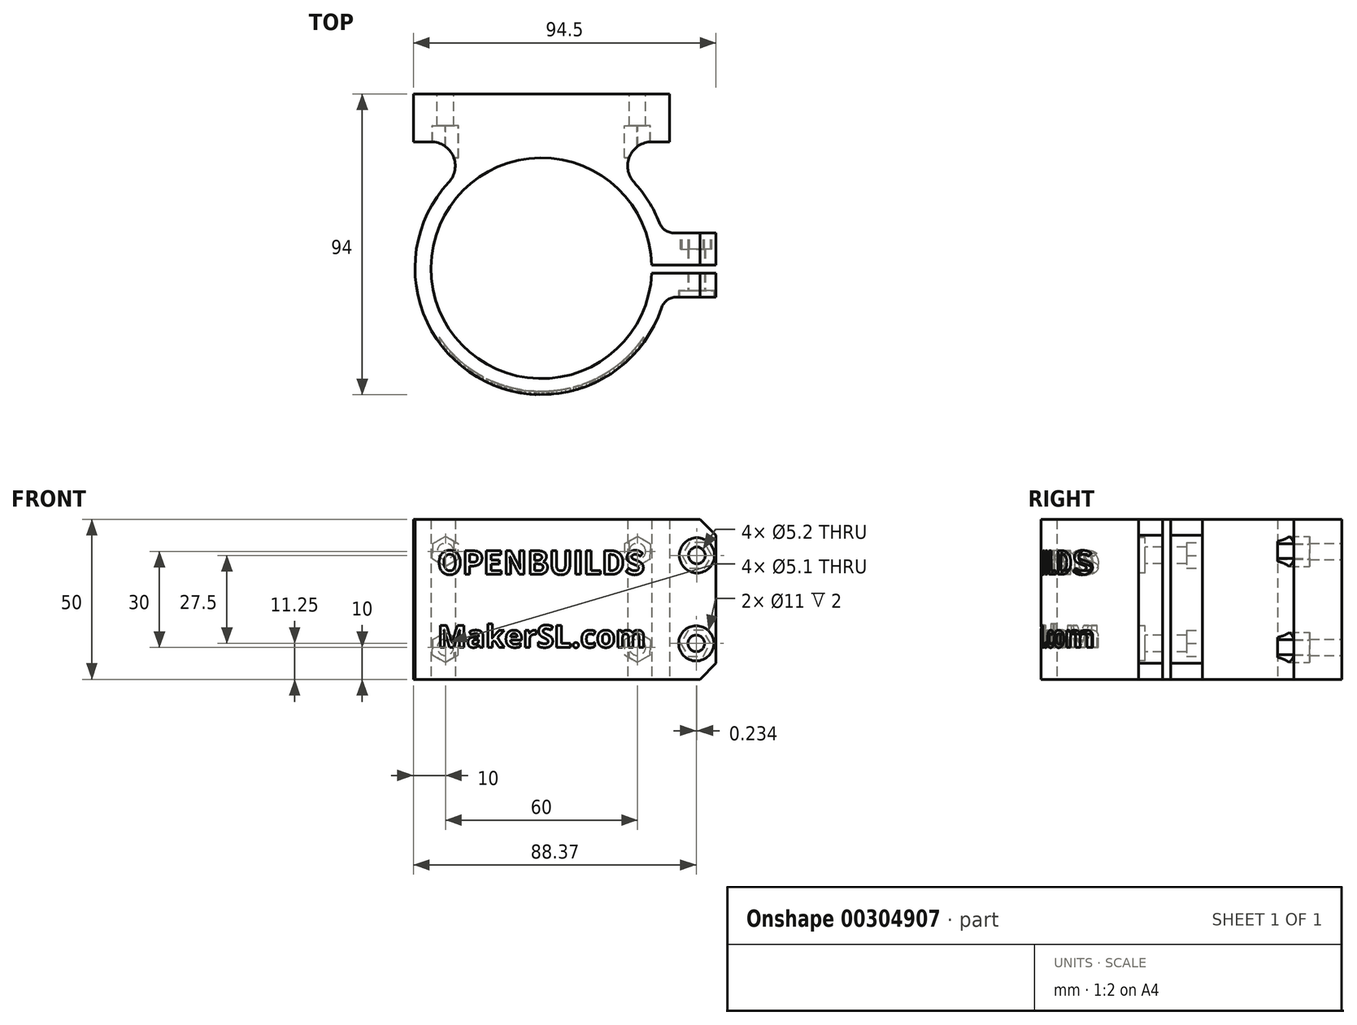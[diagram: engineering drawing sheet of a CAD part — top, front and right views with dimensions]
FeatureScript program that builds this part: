
annotation { "Feature Type Name" : "Feature", "Feature Type Description" : "" }
export const myFeature = defineFeature(function(context is Context, id is Id, definition is map)
    precondition{}
    {
        {
            var Q0;
            Q0=qCreatedBy(makeId("Top.planeOp"),FACE);
            var sketch = newSketch(context, id + "F0", { "sketchPlane" : qUnion([Q0])});
            skArc(sketch, "E0", {"start": v(34.49, 1) * mm, "mid": v(-34.5, 0.25) * mm, "end": v(34.47, -1.5) * mm});
            skArc(sketch, "E1", {"start": v(36.86, 14.2) * mm, "mid": v(33.5, 20.93) * mm, "end": v(28.93, 26.9) * mm});
            skLineSegment(sketch, "E2.bottom", {"start": v(40, 39.5) * mm, "end": v(34.42, 39.5) * mm});
            skLineSegment(sketch, "E2.top", {"start": v(40, 54.5) * mm, "end": v(-40, 54.5) * mm});
            skLineSegment(sketch, "E2.left", {"start": v(40, 39.5) * mm, "end": v(40, 54.5) * mm});
            skLineSegment(sketch, "E2.right", {"start": v(-40, 39.5) * mm, "end": v(-40, 54.5) * mm});
            skPoint(sketch, "E2.middle", {"position": v(0, 47) * mm});
            skLineSegment(sketch, "E3", {"start": v(0, 54.5) * mm, "end": v(0, 34.5) * mm});
            skLineSegment(sketch, "E4.bottom", {"start": v(54.5, -1.5) * mm, "end": v(34.47, -1.5) * mm});
            skLineSegment(sketch, "E4.top", {"start": v(54.5, 1) * mm, "end": v(34.49, 1) * mm});
            skPoint(sketch, "E4.middle", {"position": v(34.5, 0) * mm});
            skLineSegment(sketch, "E5.bottom", {"start": v(54.5, -9) * mm, "end": v(42.24, -9) * mm});
            skLineSegment(sketch, "E5.left", {"start": v(54.5, -9) * mm, "end": v(54.5, -1.5) * mm});
            skLineSegment(sketch, "E6.trimOffspring", {"start": v(54.5, 1) * mm, "end": v(54.5, 8.5) * mm});
            skPoint(sketch, "E7.visualSharp", {"position": v(38.78, 7.5) * mm});
            skPoint(sketch, "E8.visualSharp", {"position": v(38.46, -9) * mm});
            skArc(sketch, "E8.filletArc", {"start": v(42.24, -9) * mm, "mid": v(39.31, -9.95) * mm, "end": v(37.5, -12.43) * mm});
            skArc(sketch, "E9.trimOffspring", {"start": v(-28.93, 26.9) * mm, "mid": v(-20.12, -34) * mm, "end": v(37.5, -12.43) * mm});
            skLineSegment(sketch, "E10.trimOffspring", {"start": v(-34.42, 39.5) * mm, "end": v(-40, 39.5) * mm});
            skArc(sketch, "E11.filletArc", {"start": v(-28.93, 26.9) * mm, "mid": v(-27.55, 35) * mm, "end": v(-34.42, 39.5) * mm});
            skArc(sketch, "E12.filletArc", {"start": v(34.42, 39.5) * mm, "mid": v(27.55, 35) * mm, "end": v(28.93, 26.9) * mm});
            skLineSegment(sketch, "E13.top", {"start": v(54.5, 11) * mm, "end": v(41.52, 11) * mm});
            skLineSegment(sketch, "E13.left", {"start": v(54.5, 8.5) * mm, "end": v(54.5, 11) * mm});
            skPoint(sketch, "E14.visualSharp", {"position": v(37.94, 11) * mm});
            skArc(sketch, "E14.filletArc", {"start": v(36.86, 14.2) * mm, "mid": v(38.7, 11.88) * mm, "end": v(41.52, 11) * mm});
            skSolve(sketch);
        }
        {
            var Q0;
            {var subQ3=sQuery(id+"F0.wireOp",EDGE,"E2.right");Q0=makeQuery(id+"F0.imprint","IMPRINT",FACE,{"disambiguationData":[TD([[makeQuery(id+"F0.imprint","IMPRINT",EDGE,{"derivedFrom":subQ3}),-1.0]])]});}
            var Q1;
            Q1=makeQuery(id+"F0.imprint","IMPRINT",FACE,{"disambiguationData":[TD([[makeQuery(id+"F0.imprint","IMPRINT",EDGE,{"derivedFrom":sQuery(id+"F0.wireOp",EDGE,"E1")}),1.0]])]});
            extrude(context, id + "F1", {"entities" : qUnion([Q0, Q1]), "depth" : 50 * mm});
        }
        {
            var Q0;
            Q0=makeQuery(id+"F1.opExtrude","SWEPT_FACE",FACE,{"disambiguationData":[OSD([sQuery(id+"F0.wireOp",EDGE,"E2.top")])]});
            var sketch = newSketch(context, id + "F2", { "sketchPlane" : qUnion([Q0])});
            skLineSegment(sketch, "E15", {"start": v(-40, 10) * mm, "end": v(40, 10) * mm, "construction": true});
            skLineSegment(sketch, "E16", {"start": v(-40, 40) * mm, "end": v(40, 40) * mm, "construction": true});
            skCircle(sketch, "E17", {"center": v(-30, 10) * mm, "radius": 2.55 * mm});
            skCircle(sketch, "E18", {"center": v(-30, 40) * mm, "radius": 2.55 * mm});
            skCircle(sketch, "E19", {"center": v(30, 40) * mm, "radius": 2.55 * mm});
            skCircle(sketch, "E20", {"center": v(30, 10) * mm, "radius": 2.55 * mm});
            skSolve(sketch);
        }
        {
            var Q0;
            Q0=qSketchRegion(id+"F2",true);
            extrude(context, id + "F3", {"entities" : qUnion([Q0]), "operationType" : NewBodyOperationType.REMOVE, "oppositeDirection" : true, "depth" : 15 * mm});
        }
        {
            var Q0;
            Q0=qCreatedBy(makeId("Front.planeOp"),FACE);
            var sketch = newSketch(context, id + "F4", { "sketchPlane" : qUnion([Q0])});
            skLineSegment(sketch, "E21", {"start": v(0, 25) * mm, "end": v(57.85, 25) * mm});
            skArc(sketch, "E22.0.startCap", {"start": v(0, 22.5) * mm, "mid": v(-2.5, 25) * mm, "end": v(0, 27.5) * mm});
            skArc(sketch, "E22.0.endCap", {"start": v(57.85, 27.5) * mm, "mid": v(60.35, 25) * mm, "end": v(57.85, 22.5) * mm});
            skLineSegment(sketch, "E22.0.left", {"start": v(0, 27.5) * mm, "end": v(57.85, 27.5) * mm});
            skLineSegment(sketch, "E22.0.right", {"start": v(0, 22.5) * mm, "end": v(57.85, 22.5) * mm});
            skSolve(sketch);
        }
        {
            var Q0;
            {var subQ2=sQuery(id+"F0.wireOp",EDGE,"E5.bottom");Q0=makeQuery(id+"FSlxkKbNy0vXjha_1.boolean.opBoolean","SPLIT",FACE,{"disambiguationData":[TD([makeQuery(id+"FSlxkKbNy0vXjha_1.opExtrude","SWEPT_FACE",FACE,{"disambiguationData":[OSD([sQuery(id+"F4.wireOp",EDGE,"E22.0.left")])]})])],"derivedFrom":makeQuery(id+"F1.opExtrude","SWEPT_FACE",FACE,{"disambiguationData":[OSD([subQ2])]})});}
            var sketch = newSketch(context, id + "F5", { "sketchPlane" : qUnion([Q0])});
            skLineSegment(sketch, "E23", {"start": v(48.37, 50) * mm, "end": v(48.37, 0) * mm, "construction": true});
            skLineSegment(sketch, "E24", {"start": v(54.5, 11.25) * mm, "end": v(42.24, 11.25) * mm, "construction": true});
            skCircle(sketch, "E25", {"center": v(48.6, 38.75) * mm, "radius": 2.6 * mm});
            skCircle(sketch, "E26", {"center": v(48.37, 11.25) * mm, "radius": 2.6 * mm});
            skCircle(sketch, "E27", {"center": v(48.6, 38.75) * mm, "radius": 2 * mm});
            skCircle(sketch, "E28", {"center": v(48.37, 11.25) * mm, "radius": 2 * mm});
            skSolve(sketch);
        }
        {
            var Q0;
            Q0=makeQuery(id+"F5.imprint","IMPRINT",FACE,{"disambiguationData":[TD([[makeQuery(id+"F5.imprint","IMPRINT",EDGE,{"derivedFrom":sQuery(id+"F5.wireOp",EDGE,"E26")}),1.0]])]});
            var Q1;
            Q1=makeQuery(id+"F5.imprint","IMPRINT",FACE,{"disambiguationData":[TD([[makeQuery(id+"F5.imprint","IMPRINT",EDGE,{"derivedFrom":sQuery(id+"F5.wireOp",EDGE,"E25")}),1.0]])]});
            var Q2;
            Q2=makeQuery(id+"F5.imprint","IMPRINT",FACE,{"disambiguationData":[TD([[makeQuery(id+"F5.imprint","IMPRINT",EDGE,{"derivedFrom":sQuery(id+"F5.wireOp",EDGE,"E27")}),1.0]])]});
            var Q3;
            Q3=makeQuery(id+"F5.imprint","IMPRINT",FACE,{"disambiguationData":[TD([[makeQuery(id+"F5.imprint","IMPRINT",EDGE,{"derivedFrom":sQuery(id+"F5.wireOp",EDGE,"E28")}),1.0]])]});
            var Q4;
            {var subQ2=sQuery(id+"F0.wireOp",EDGE,"E4.bottom");Q4=makeQuery(id+"FSlxkKbNy0vXjha_1.boolean.opBoolean","SPLIT",FACE,{"disambiguationData":[TD([makeQuery(id+"FSlxkKbNy0vXjha_1.opExtrude","SWEPT_FACE",FACE,{"disambiguationData":[OSD([sQuery(id+"F4.wireOp",EDGE,"E22.0.right")])]})])],"derivedFrom":makeQuery(id+"F1.opExtrude","SWEPT_FACE",FACE,{"disambiguationData":[OSD([subQ2])]})});}
            extrude(context, id + "F6", {"entities" : qUnion([Q0, Q1, Q2, Q3]), "operationType" : NewBodyOperationType.REMOVE, "endBound" : BoundingType.THROUGH_ALL, "oppositeDirection" : true, "endBoundEntityFace" : qUnion([Q4]), "depth" : 25 * mm});
        }
        {
            var Q0;
            Q0=qCreatedBy(makeId("Right.planeOp"),FACE);
            var sketch = newSketch(context, id + "F7", { "sketchPlane" : qUnion([Q0])});
            skLineSegment(sketch, "E29", {"start": v(-2.5, 25) * mm, "end": v(-48.95, 25) * mm});
            skArc(sketch, "E30.0.startCap", {"start": v(-2.5, 27.5) * mm, "mid": v(0, 25) * mm, "end": v(-2.5, 22.5) * mm});
            skArc(sketch, "E30.0.endCap", {"start": v(-48.95, 22.5) * mm, "mid": v(-51.45, 25) * mm, "end": v(-48.95, 27.5) * mm});
            skLineSegment(sketch, "E30.0.left", {"start": v(-2.5, 22.5) * mm, "end": v(-48.95, 22.5) * mm});
            skLineSegment(sketch, "E30.0.right", {"start": v(-2.5, 27.5) * mm, "end": v(-48.95, 27.5) * mm});
            skSolve(sketch);
        }
        {
            var Q0;
            Q0=makeQuery(id+"F1.opExtrude","SWEPT_FACE",FACE,{"disambiguationData":[OSD([sQuery(id+"F0.wireOp",EDGE,"E2.top")])]});
            cPlane(context, id + "F8", {"entities" : qUnion([Q0]), "cplaneType" : CPlaneType.OFFSET, "offset" : 10 * mm, "oppositeDirection" : true, "width" : 150 * mm, "height" : 150 * mm});
        }
        {
            var Q0;
            Q0=qCreatedBy(id+"F8.planeOp",FACE);
            var sketch = newSketch(context, id + "F9", { "sketchPlane" : qUnion([Q0])});
            skCircle(sketch, "E31.cCircle", {"center": v(-30, 10) * mm, "radius": 4.05 * mm, "construction": true});
            skLineSegment(sketch, "E31.0", {"start": v(-26, 12.42) * mm, "end": v(-25.9, 7.75) * mm});
            skLineSegment(sketch, "E31.1", {"start": v(-25.9, 7.75) * mm, "end": v(-29.9, 5.32) * mm});
            skLineSegment(sketch, "E31.2", {"start": v(-29.9, 5.32) * mm, "end": v(-34, 7.58) * mm});
            skLineSegment(sketch, "E31.3", {"start": v(-34, 7.58) * mm, "end": v(-34.1, 12.25) * mm});
            skLineSegment(sketch, "E31.4", {"start": v(-34.1, 12.25) * mm, "end": v(-30.1, 14.68) * mm});
            skLineSegment(sketch, "E31.5", {"start": v(-30.1, 14.68) * mm, "end": v(-26, 12.42) * mm});
            skPoint(sketch, "E31.0.midPoint", {"position": v(-25.95, 10.09) * mm});
            skCircle(sketch, "E32.0.1.0", {"center": v(-30, 40) * mm, "radius": 4.05 * mm, "construction": true});
            skLineSegment(sketch, "E32.0.1.1", {"start": v(-25.9, 37.75) * mm, "end": v(-29.9, 35.32) * mm});
            skLineSegment(sketch, "E32.0.1.2", {"start": v(-30.1, 44.68) * mm, "end": v(-26, 42.42) * mm});
            skPoint(sketch, "E32.0.1.3", {"position": v(-25.95, 40.09) * mm});
            skLineSegment(sketch, "E32.0.1.4", {"start": v(-29.9, 35.32) * mm, "end": v(-34, 37.58) * mm});
            skLineSegment(sketch, "E32.0.1.5", {"start": v(-34.1, 42.25) * mm, "end": v(-30.1, 44.68) * mm});
            skLineSegment(sketch, "E32.0.1.6", {"start": v(-26, 42.42) * mm, "end": v(-25.9, 37.75) * mm});
            skLineSegment(sketch, "E32.0.1.7", {"start": v(-34, 37.58) * mm, "end": v(-34.1, 42.25) * mm});
            skCircle(sketch, "E32.1.0.0", {"center": v(30, 10) * mm, "radius": 4.05 * mm, "construction": true});
            skLineSegment(sketch, "E32.1.0.1", {"start": v(34.1, 7.75) * mm, "end": v(30.1, 5.32) * mm});
            skLineSegment(sketch, "E32.1.0.2", {"start": v(29.9, 14.68) * mm, "end": v(34, 12.42) * mm});
            skPoint(sketch, "E32.1.0.3", {"position": v(34.05, 10.09) * mm});
            skLineSegment(sketch, "E32.1.0.4", {"start": v(30.1, 5.32) * mm, "end": v(26, 7.58) * mm});
            skLineSegment(sketch, "E32.1.0.5", {"start": v(25.9, 12.25) * mm, "end": v(29.9, 14.68) * mm});
            skLineSegment(sketch, "E32.1.0.6", {"start": v(34, 12.42) * mm, "end": v(34.1, 7.75) * mm});
            skLineSegment(sketch, "E32.1.0.7", {"start": v(26, 7.58) * mm, "end": v(25.9, 12.25) * mm});
            skCircle(sketch, "E32.1.1.0", {"center": v(30, 40) * mm, "radius": 4.05 * mm, "construction": true});
            skLineSegment(sketch, "E32.1.1.1", {"start": v(34.1, 37.75) * mm, "end": v(30.1, 35.32) * mm});
            skLineSegment(sketch, "E32.1.1.2", {"start": v(29.9, 44.68) * mm, "end": v(34, 42.42) * mm});
            skPoint(sketch, "E32.1.1.3", {"position": v(34.05, 40.09) * mm});
            skLineSegment(sketch, "E32.1.1.4", {"start": v(30.1, 35.32) * mm, "end": v(26, 37.58) * mm});
            skLineSegment(sketch, "E32.1.1.5", {"start": v(25.9, 42.25) * mm, "end": v(29.9, 44.68) * mm});
            skLineSegment(sketch, "E32.1.1.6", {"start": v(34, 42.42) * mm, "end": v(34.1, 37.75) * mm});
            skLineSegment(sketch, "E32.1.1.7", {"start": v(26, 37.58) * mm, "end": v(25.9, 42.25) * mm});
            skLineSegment(sketch, "E32.direction1", {"start": v(-34, 7.58) * mm, "end": v(26, 7.58) * mm, "construction": true});
            skLineSegment(sketch, "E32.direction2", {"start": v(-34, 7.58) * mm, "end": v(-34, 37.58) * mm, "construction": true});
            skSolve(sketch);
        }
        {
            var Q0;
            Q0 = qSketchRegion(id + "F9", true);
            extrude(context, id + "F10", {"entities" : qUnion([Q0]), "operationType" : NewBodyOperationType.REMOVE, "oppositeDirection" : true, "depth" : 10 * mm});
        }
        {
            var Q0;
            Q0=makeQuery(id+"F1.opExtrude","SWEPT_FACE",FACE,{"disambiguationData":[OSD([sQuery(id+"F0.wireOp",EDGE,"E13.top")])]});
            var sketch = newSketch(context, id + "F11", { "sketchPlane" : qUnion([Q0])});
            skCircle(sketch, "E33.cCircle", {"center": v(-48.6, 38.75) * mm, "radius": 4.05 * mm, "construction": true});
            skLineSegment(sketch, "E33.0", {"start": v(-43.93, 38.75) * mm, "end": v(-46.27, 34.7) * mm});
            skLineSegment(sketch, "E33.1", {"start": v(-46.27, 34.7) * mm, "end": v(-50.94, 34.7) * mm});
            skLineSegment(sketch, "E33.2", {"start": v(-50.94, 34.7) * mm, "end": v(-53.28, 38.75) * mm});
            skLineSegment(sketch, "E33.3", {"start": v(-53.28, 38.75) * mm, "end": v(-50.94, 42.8) * mm});
            skLineSegment(sketch, "E33.4", {"start": v(-50.94, 42.8) * mm, "end": v(-46.27, 42.8) * mm});
            skLineSegment(sketch, "E33.5", {"start": v(-46.27, 42.8) * mm, "end": v(-43.93, 38.75) * mm});
            skPoint(sketch, "E33.0.midPoint", {"position": v(-45.1, 36.73) * mm});
            skCircle(sketch, "E34.cCircle", {"center": v(-48.2, 11.25) * mm, "radius": 4.05 * mm, "construction": true});
            skLineSegment(sketch, "E34.0", {"start": v(-43.52, 11.25) * mm, "end": v(-45.86, 7.2) * mm});
            skLineSegment(sketch, "E34.1", {"start": v(-45.86, 7.2) * mm, "end": v(-50.54, 7.2) * mm});
            skLineSegment(sketch, "E34.2", {"start": v(-50.54, 7.2) * mm, "end": v(-52.87, 11.25) * mm});
            skLineSegment(sketch, "E34.3", {"start": v(-52.87, 11.25) * mm, "end": v(-50.54, 15.3) * mm});
            skLineSegment(sketch, "E34.4", {"start": v(-50.54, 15.3) * mm, "end": v(-45.86, 15.3) * mm});
            skLineSegment(sketch, "E34.5", {"start": v(-45.86, 15.3) * mm, "end": v(-43.52, 11.25) * mm});
            skPoint(sketch, "E34.0.midPoint", {"position": v(-44.7, 9.22) * mm});
            skSolve(sketch);
        }
        {
            var Q0;
            Q0 = qSketchRegion(id + "F11", true);
            extrude(context, id + "F12", {"entities" : qUnion([Q0]), "operationType" : NewBodyOperationType.REMOVE, "oppositeDirection" : true, "depth" : 5 * mm});
        }
        {
            var Q0;
            Q0=qCreatedBy(makeId("Front.planeOp"),FACE);
            cPlane(context, id + "F13", {"entities" : qUnion([Q0]), "cplaneType" : CPlaneType.OFFSET, "offset" : 50 * mm, "width" : 150 * mm, "height" : 150 * mm});
        }
        {
            var Q0;
            Q0=qCreatedBy(id+"F13.planeOp",FACE);
            var sketch = newSketch(context, id + "F14", { "sketchPlane" : qUnion([Q0])});
            skText(sketch, "E35", { "text": "OPENBUILDS", "fontName": "NotoSansCJKsc-Bold.otf"});
            skText(sketch, "E36", { "text": "MakerSL.com", "fontName": "OpenSans-Bold.ttf"});
            const initialGuessF14  = {"E35": [-0.0325, 0.0328, 1, 0, 0.0072], "E36": [-0.0325, 0.01, 1, 0, 0.00697]};
            skSetInitialGuess(sketch, initialGuessF14);
            skSolve(sketch);
        }
        {
            var Q0;
            Q0 = qSketchRegion(id + "F14", true);
            extrude(context, id + "F15", {"entities" : qUnion([Q0]), "operationType" : NewBodyOperationType.REMOVE, "oppositeDirection" : true, "depth" : 50 * mm});
        }
        {
            var Q0;
            Q0=makeQuery(id+"F1.opExtrude","CAP_FACE",FACE,{"disambiguationData":[OSD([sQuery(id+"F0.wireOp",EDGE,"E0"),sQuery(id+"F0.wireOp",EDGE,"E1"),sQuery(id+"F0.wireOp",EDGE,"E2.bottom"),sQuery(id+"F0.wireOp",EDGE,"E2.top"),sQuery(id+"F0.wireOp",EDGE,"E2.left"),sQuery(id+"F0.wireOp",EDGE,"E2.right"),sQuery(id+"F0.wireOp",EDGE,"E4.bottom"),sQuery(id+"F0.wireOp",EDGE,"E4.top"),sQuery(id+"F0.wireOp",EDGE,"E5.bottom"),sQuery(id+"F0.wireOp",EDGE,"E5.left"),sQuery(id+"F0.wireOp",EDGE,"E6.trimOffspring"),sQuery(id+"F0.wireOp",EDGE,"E8.filletArc"),sQuery(id+"F0.wireOp",EDGE,"E9.trimOffspring"),sQuery(id+"F0.wireOp",EDGE,"E10.trimOffspring"),sQuery(id+"F0.wireOp",EDGE,"E11.filletArc"),sQuery(id+"F0.wireOp",EDGE,"E12.filletArc"),sQuery(id+"F0.wireOp",EDGE,"E13.top"),sQuery(id+"F0.wireOp",EDGE,"E13.left"),sQuery(id+"F0.wireOp",EDGE,"E14.filletArc")])],"isStart":false});
            var sketch = newSketch(context, id + "F16", { "sketchPlane" : qUnion([Q0])});
            skArc(sketch, "E37", {"start": v(-34.5, 0) * mm, "mid": v(-2.28, -34.42) * mm, "end": v(34.2, -4.54) * mm});
            skArc(sketch, "E38", {"start": v(-38.5, 0) * mm, "mid": v(-2.54, -38.42) * mm, "end": v(38.16, -5.07) * mm});
            skLineSegment(sketch, "E39", {"start": v(-34.5, 0) * mm, "end": v(-38.5, 0) * mm});
            skLineSegment(sketch, "E40", {"start": v(34.2, -4.54) * mm, "end": v(38.16, -5.07) * mm});
            skSolve(sketch);
        }
        {
            var Q0;
            Q0=makeQuery(id+"F16.imprint","IMPRINT",FACE,{"disambiguationData":[TD([[makeQuery(id+"F16.imprint","IMPRINT",EDGE,{"derivedFrom":sQuery(id+"F16.wireOp",EDGE,"E37")}),-1.0]])]});
            extrude(context, id + "F17", {"entities" : qUnion([Q0]), "operationType" : NewBodyOperationType.ADD, "oppositeDirection" : true, "depth" : 49 * mm});
        }
        {
            var Q0;
            Q0=makeQuery(id+"F1.opExtrude","CAP_EDGE",EDGE,{"disambiguationData":[OSD([sQuery(id+"F0.wireOp",EDGE,"E5.left")])],"isStart":false});
            var Q1;
            Q1=makeQuery(id+"F1.opExtrude","CAP_EDGE",EDGE,{"disambiguationData":[OSD([sQuery(id+"F0.wireOp",EDGE,"E6.trimOffspring"),sQuery(id+"F0.wireOp",EDGE,"E13.left")])],"isStart":false});
            var Q2;
            Q2=makeQuery(id+"F1.opExtrude","CAP_EDGE",EDGE,{"disambiguationData":[OSD([sQuery(id+"F0.wireOp",EDGE,"E6.trimOffspring"),sQuery(id+"F0.wireOp",EDGE,"E13.left")])],"isStart":true});
            var Q3;
            Q3=makeQuery(id+"F1.opExtrude","CAP_EDGE",EDGE,{"disambiguationData":[OSD([sQuery(id+"F0.wireOp",EDGE,"E5.left")])],"isStart":true});
            chamfer(context, id + "F18", {"entities" : qUnion([Q0, Q1, Q2, Q3]), "width" : 5 * mm, "tangentPropagation" : true});
        }
        {
            var Q0;
            Q0=qCreatedBy(makeId("Right.planeOp"),FACE);
            cPlane(context, id + "F19", {"entities" : qUnion([Q0]), "cplaneType" : CPlaneType.OFFSET, "offset" : 50 * mm, "oppositeDirection" : true, "width" : 150 * mm, "height" : 150 * mm});
        }
        {
            var Q0;
            Q0=makeQuery(id+"F1.opExtrude","SWEPT_FACE",FACE,{"disambiguationData":[OSD([sQuery(id+"F0.wireOp",EDGE,"E5.bottom")])]});
            var sketch = newSketch(context, id + "F20", { "sketchPlane" : qUnion([Q0])});
            skCircle(sketch, "E41", {"center": v(48.6, 38.75) * mm, "radius": 5.5 * mm});
            skCircle(sketch, "E42", {"center": v(48.37, 11.25) * mm, "radius": 5.5 * mm});
            skSolve(sketch);
        }
        {
            var Q0;
            Q0=makeQuery(id+"F20.imprint","IMPRINT",FACE,{"disambiguationData":[TD([[makeQuery(id+"F20.imprint","IMPRINT",EDGE,{"derivedFrom":sQuery(id+"F20.wireOp",EDGE,"E41")}),1.0]])]});
            var Q1;
            Q1=makeQuery(id+"F20.imprint","IMPRINT",FACE,{"disambiguationData":[TD([[makeQuery(id+"F20.imprint","IMPRINT",EDGE,{"derivedFrom":sQuery(id+"F20.wireOp",EDGE,"E42")}),1.0]])]});
            extrude(context, id + "F21", {"entities" : qUnion([Q0, Q1]), "operationType" : NewBodyOperationType.REMOVE, "oppositeDirection" : true, "depth" : 2 * mm});
        }
    });
